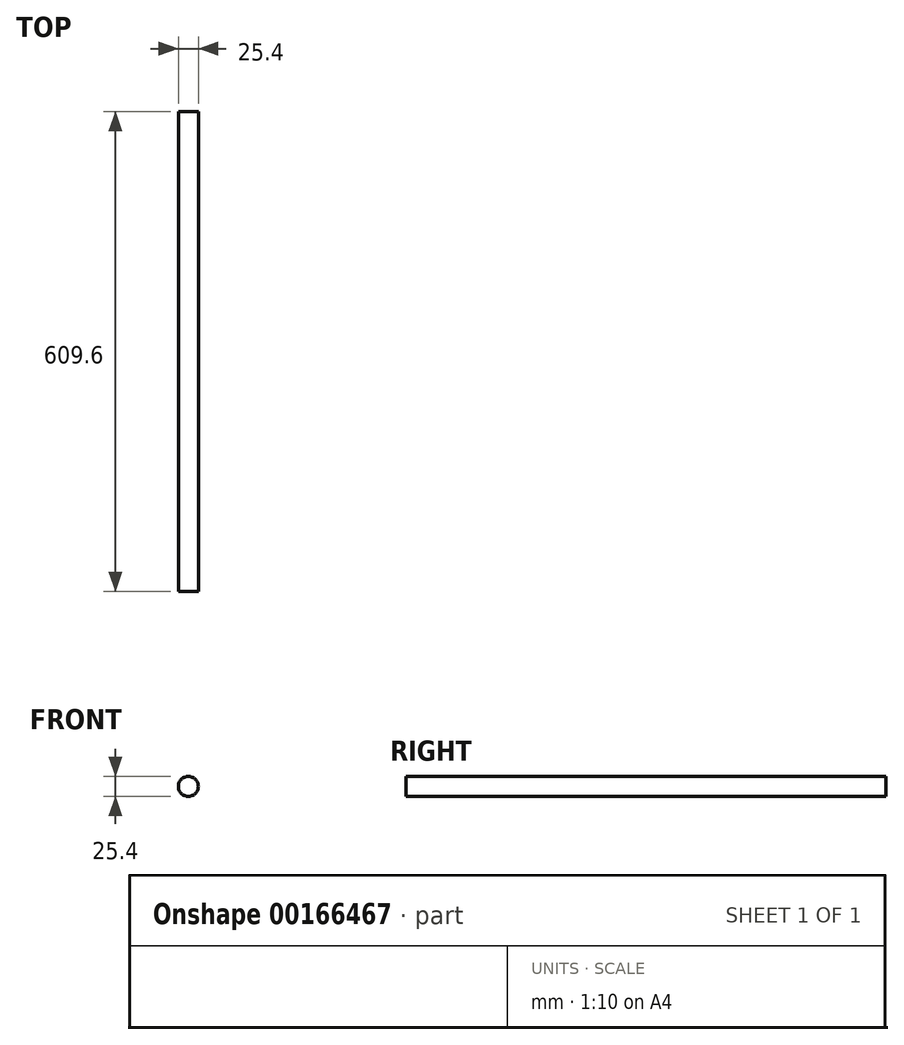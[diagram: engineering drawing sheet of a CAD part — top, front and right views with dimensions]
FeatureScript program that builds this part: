
annotation { "Feature Type Name" : "Feature", "Feature Type Description" : "" }
export const myFeature = defineFeature(function(context is Context, id is Id, definition is map)
    precondition{}
    {
        {
            var Q0;
            Q0=qCreatedBy(makeId("Front.planeOp"),FACE);
            var sketch = newSketch(context, id + "F0", { "sketchPlane" : qUnion([Q0])});
            skCircle(sketch, "E0", {"center": v(0, 0) * mm, "radius": 12.7 * mm});
            skCircle(sketch, "E1", {"center": v(0, 0) * mm, "radius": 12.07 * mm});
            skSolve(sketch);
        }
        {
            var Q0;
            Q0=sQuery(id+"F0.wireOp",EDGE,"E0");
            extrude(context, id + "F1", {"bodyType" : ToolBodyType.SURFACE, "surfaceEntities" : qUnion([Q0]), "depth" : 609.6 * mm});
        }
    });
